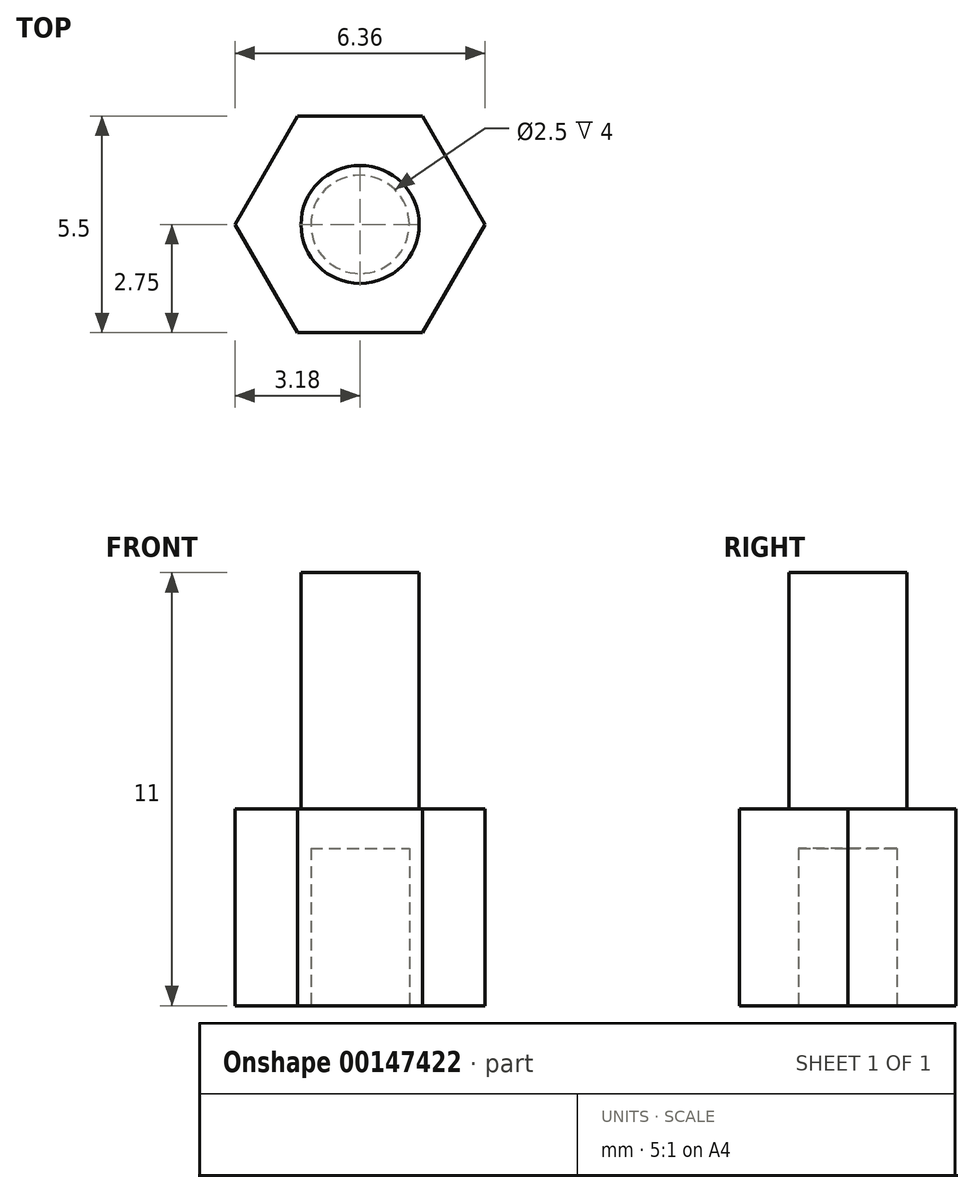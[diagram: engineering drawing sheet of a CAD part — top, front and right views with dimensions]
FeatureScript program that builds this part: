
annotation { "Feature Type Name" : "Feature", "Feature Type Description" : "" }
export const myFeature = defineFeature(function(context is Context, id is Id, definition is map)
    precondition{}
    {
        {
            var Q0;
            Q0=qCreatedBy(makeId("Top.planeOp"),FACE);
            var sketch = newSketch(context, id + "F0", { "sketchPlane" : qUnion([Q0])});
            skCircle(sketch, "E0.cCircle", {"center": v(0, 0) * mm, "radius": 2.75 * mm, "construction": true});
            skLineSegment(sketch, "E0.0", {"start": v(-1.59, 2.75) * mm, "end": v(1.59, 2.75) * mm});
            skLineSegment(sketch, "E0.1", {"start": v(1.59, 2.75) * mm, "end": v(3.18, 0) * mm});
            skLineSegment(sketch, "E0.2", {"start": v(3.18, 0) * mm, "end": v(1.59, -2.75) * mm});
            skLineSegment(sketch, "E0.3", {"start": v(1.59, -2.75) * mm, "end": v(-1.59, -2.75) * mm});
            skLineSegment(sketch, "E0.4", {"start": v(-1.59, -2.75) * mm, "end": v(-3.18, 0) * mm});
            skLineSegment(sketch, "E0.5", {"start": v(-3.18, 0) * mm, "end": v(-1.59, 2.75) * mm});
            skPoint(sketch, "E0.0.midPoint", {"position": v(0, 2.75) * mm});
            skSolve(sketch);
        }
        {
            var Q0;
            Q0=makeQuery(id+"F0.imprint","IMPRINT",FACE,{"disambiguationData":[TD([[makeQuery(id+"F0.imprint","IMPRINT",EDGE,{"derivedFrom":sQuery(id+"F0.wireOp",EDGE,"E0.0")}),-1.0]])]});
            extrude(context, id + "F1", {"entities" : qUnion([Q0]), "depth" : 5 * mm});
        }
        {
            var Q0;
            Q0=makeQuery(id+"F1.opExtrude","CAP_FACE",FACE,{"disambiguationData":[OSD([sQuery(id+"F0.wireOp",EDGE,"E0.0"),sQuery(id+"F0.wireOp",EDGE,"E0.1"),sQuery(id+"F0.wireOp",EDGE,"E0.2"),sQuery(id+"F0.wireOp",EDGE,"E0.3"),sQuery(id+"F0.wireOp",EDGE,"E0.4"),sQuery(id+"F0.wireOp",EDGE,"E0.5")])],"isStart":false});
            var sketch = newSketch(context, id + "F2", { "sketchPlane" : qUnion([Q0])});
            skCircle(sketch, "E1", {"center": v(0, 0) * mm, "radius": 1.5 * mm});
            skSolve(sketch);
        }
        {
            var Q0;
            Q0=makeQuery(id+"F2.imprint","IMPRINT",FACE,{"disambiguationData":[TD([[makeQuery(id+"F2.imprint","IMPRINT",EDGE,{"derivedFrom":sQuery(id+"F2.wireOp",EDGE,"E1")}),1.0]])]});
            extrude(context, id + "F3", {"entities" : qUnion([Q0]), "operationType" : NewBodyOperationType.ADD, "depth" : 6 * mm});
        }
        {
            var Q0;
            Q0=makeQuery(id+"F1.opExtrude","CAP_FACE",FACE,{"disambiguationData":[OSD([sQuery(id+"F0.wireOp",EDGE,"E0.0"),sQuery(id+"F0.wireOp",EDGE,"E0.1"),sQuery(id+"F0.wireOp",EDGE,"E0.2"),sQuery(id+"F0.wireOp",EDGE,"E0.3"),sQuery(id+"F0.wireOp",EDGE,"E0.4"),sQuery(id+"F0.wireOp",EDGE,"E0.5")])],"isStart":true});
            var sketch = newSketch(context, id + "F4", { "sketchPlane" : qUnion([Q0])});
            skCircle(sketch, "E2", {"center": v(0, 0) * mm, "radius": 1.25 * mm});
            skSolve(sketch);
        }
        {
            var Q0;
            Q0=makeQuery(id+"F4.imprint","IMPRINT",FACE,{"disambiguationData":[TD([[makeQuery(id+"F4.imprint","IMPRINT",EDGE,{"derivedFrom":sQuery(id+"F4.wireOp",EDGE,"E2")}),1.0]])]});
            extrude(context, id + "F5", {"entities" : qUnion([Q0]), "operationType" : NewBodyOperationType.REMOVE, "oppositeDirection" : true, "depth" : 4 * mm});
        }
    });
